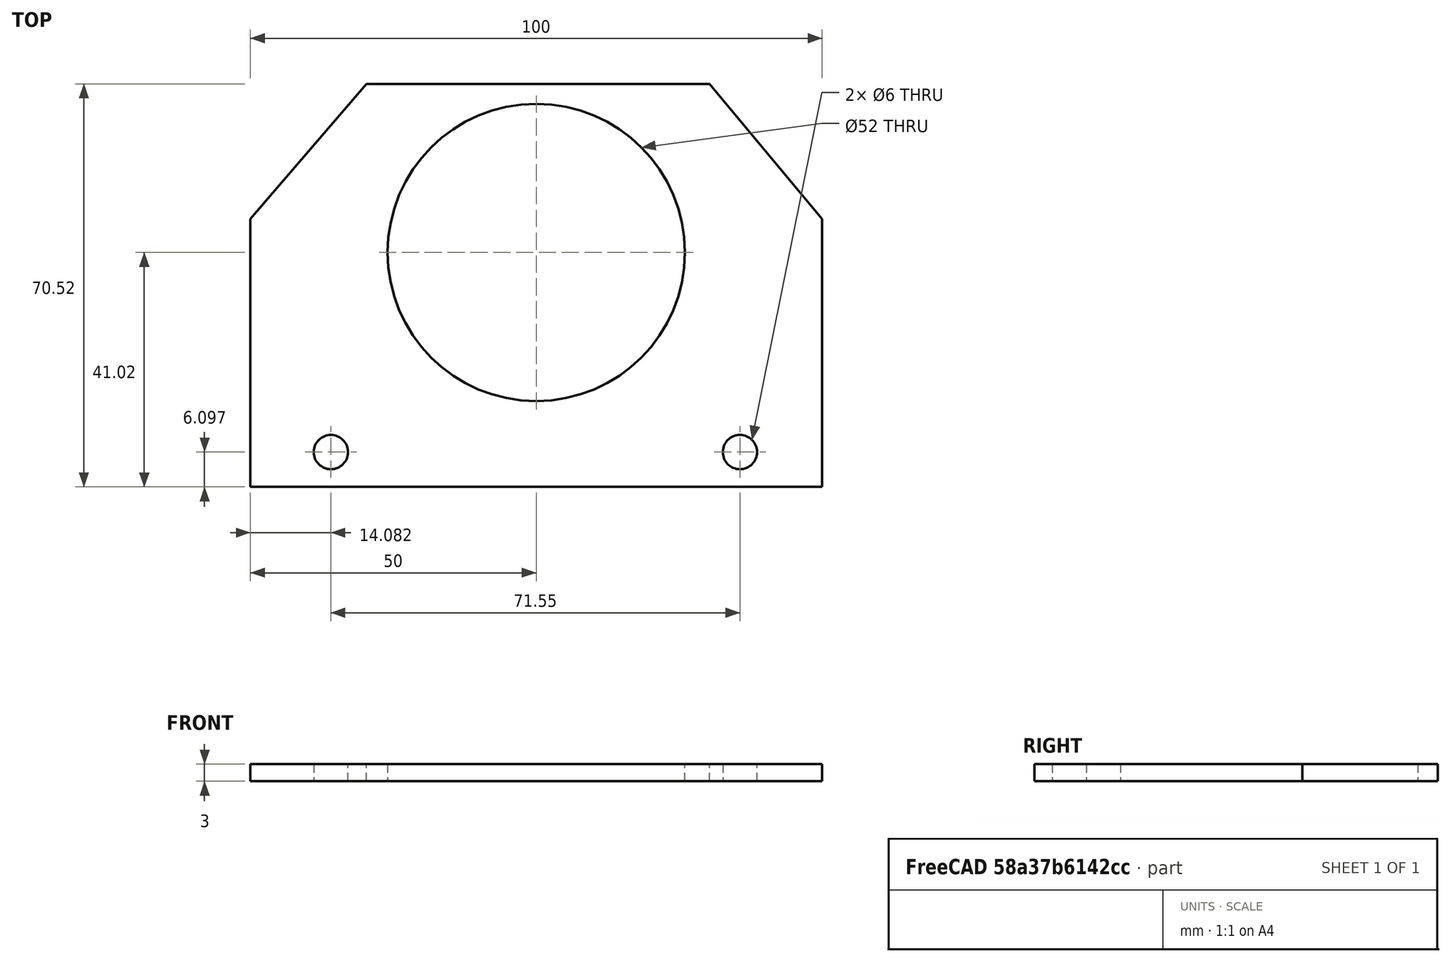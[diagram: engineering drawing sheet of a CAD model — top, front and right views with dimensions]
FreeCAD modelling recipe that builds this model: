
FCSTD DOCUMENT  (FreeCAD 0.18R16131 (Git))
Label: Resin_Slot
License: All rights reserved
LicenseURL: http://en.wikipedia.org/wiki/All_rights_reserved
objects: Sketcher::SketchObject×1, PartDesign::Pad×1, PartDesign::Body×1
note: 4 computed .brp shape members not serialized (recipe doc carries the construction recipe); baked Part::Feature solids carry a one-line shape summary decoded from their .brp

FEATURE [Sketcher::SketchObject] Sketch
  MapMode = 5
  Support = -> [XY_Plane]
  sketch-geometry (9):
    g0: LineSegment StartX=-50 StartY=-41.0193 StartZ=0 EndX=50 EndY=-41.0193 EndZ=0
    g1: LineSegment StartX=50 StartY=-41.0193 StartZ=0 EndX=50 EndY=5.85069 EndZ=0
    g2: LineSegment StartX=-29.6763 StartY=29.5037 StartZ=0 EndX=30.3237 EndY=29.5037 EndZ=0
    g3: LineSegment StartX=-50 StartY=-41.0193 StartZ=0 EndX=-50 EndY=5.85069 EndZ=0
    g4: LineSegment StartX=-50 StartY=5.85069 StartZ=0 EndX=-29.6763 EndY=29.5037 EndZ=0
    g5: LineSegment StartX=30.3237 StartY=29.5037 StartZ=0 EndX=50 EndY=5.85069 EndZ=0
    g6: Circle CenterX=-35.9179 CenterY=-34.9229 CenterZ=0 NormalX=0 NormalY=0 NormalZ=1 AngleXU=0 Radius=3
    g7: Circle CenterX=35.6321 CenterY=-34.9229 CenterZ=0 NormalX=0 NormalY=0 NormalZ=1 AngleXU=0 Radius=3
    g8: Circle CenterX=0 CenterY=0 CenterZ=0 NormalX=0 NormalY=0 NormalZ=1 AngleXU=0 Radius=26
  constraints (21):
    c: Horizontal(g0)
    c: Coincident(g1,g0)
    c: Vertical(g1)
    c: Horizontal(g2)
    c: DistanceX(g0,g0) = 100
    c: DistanceX(g-1,g0) = 50
    c: DistanceY(g1,g1) = 46.87
    c: Coincident(g3,g0)
    c: Vertical(g3)
    c: DistanceY(g3,g3) = 46.87
    c: DistanceX(g2,g2) = 60
    c: Coincident(g4,g3)
    c: Coincident(g4,g2)
    c: Coincident(g5,g2)
    c: Coincident(g5,g1)
    c: Radius(g6) = 3
    c: Equal(g6,g7) = 3
    c: Horizontal(g6,g7)
    c: DistanceX(g6,g7) = 71.55
    c: Coincident(g8,g-1)
    c: Radius(g8) = 26
FEATURE [PartDesign::Pad] Pad
  Length = 3
  Length2 = 100
  Profile = -> Sketch
  Type = 0
FEATURE [PartDesign::Body] Body
  Group = -> [Sketch,Pad]
  Origin = -> Origin
  Tip = -> Pad
